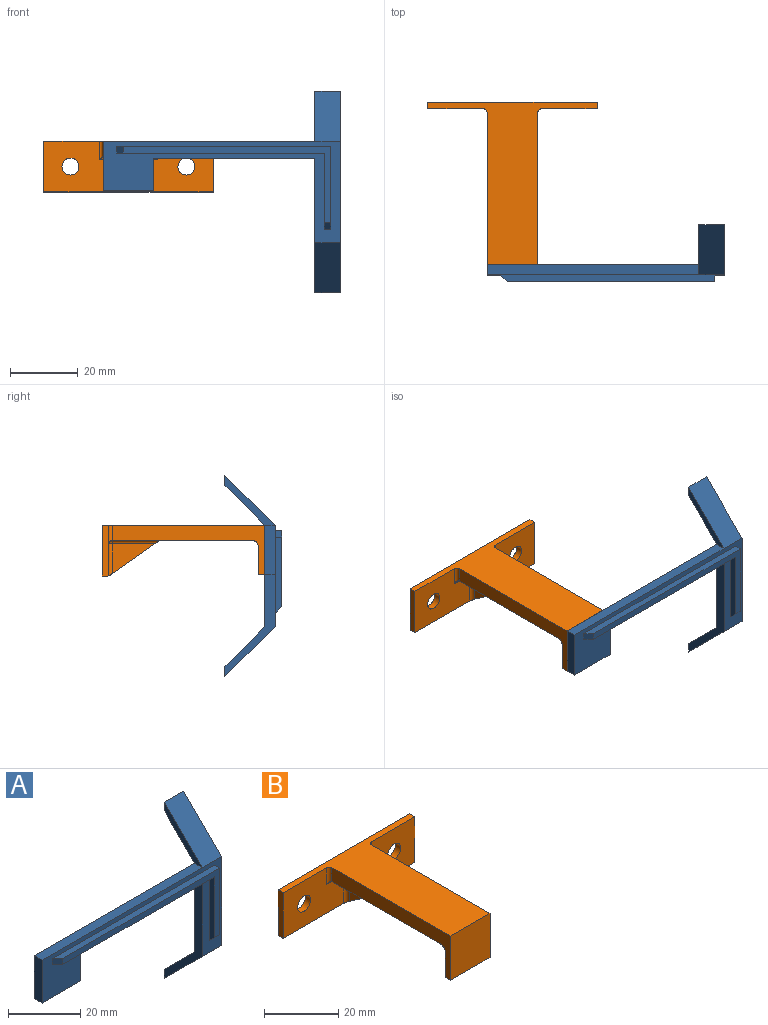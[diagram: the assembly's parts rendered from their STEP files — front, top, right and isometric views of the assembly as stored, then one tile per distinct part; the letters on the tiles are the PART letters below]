
ASSEMBLY  parts=2 mates=1
PART A: 23 faces, bbox 70x16.8x59.6 mm
  f0: plane 59.56x14.78mm, normal (1,0,0), area 169.7mm2, adj f2,f3,f4,f5,f12,f20,f21,f22
  f1: plane 14.78x14.78mm, normal (-1,0,0), area 39.8mm2, adj f2,f3,f4,f6
  f2: plane 11.78x11.78mm, normal (0,0.71,-0.71), area 124.9mm2, adj f0,f1,f4,f12
  f3: plane 14.78x14.78mm, normal (0,-0.71,0.71), area 156.8mm2, adj f0,f1,f4,f5
  f4: plane 7.5x3mm, normal (0,1,0), area 22.5mm2, adj f0,f1,f2,f3
  f5: plane 70x30mm, normal (0,-1,0), area 508.5mm2, adj f0,f3,f6,f7,f8,f9,f10,f11
  f6: plane 62.5x3mm, normal (0,0,1), area 187.5mm2, adj f1,f5,f7,f12
  f7: plane 14.5x3mm, normal (-1,0,0), area 43.5mm2, adj f5,f6,f8,f12
  f8: plane 15x3mm, normal (0,0,-1), area 45mm2, adj f5,f7,f9,f12
  f9: plane 9.5x3mm, normal (1,0,0), area 28.5mm2, adj f5,f8,f10,f12
  f10: plane 47.5x3mm, normal (0,0,-1), area 142.5mm2, adj f5,f9,f11,f12
  f11: plane 39.78x14.78mm, normal (-1,0,0), area 114.8mm2, adj f5,f10,f12,f20,f21,f22
  f12: plane 70x30mm, normal (0,1,0), area 680mm2, adj f0,f2,f6,f7,f8,f9,f10,f11
  f13: plane 63.25x2mm, normal (0,0,1), area 124.5mm2, adj f5,f16,f17,f19
  f14: plane 61.25x2mm, normal (0,0,-1), area 120.5mm2, adj f5,f15,f17,f19
  f15: plane 22.5x2mm, normal (-1,0,0), area 43mm2, adj f5,f14,f17,f18
  f16: plane 24.5x2mm, normal (1,0,0), area 47mm2, adj f5,f13,f17,f18
  f17: plane 61.25x22.5mm, normal (0,-1,0), area 163.5mm2, adj f13,f14,f15,f16,f18,f19
  f18: plane 2x2mm, normal (0,-0.71,-0.71), area 5.7mm2, adj f5,f15,f16,f17
  f19: plane 2x2mm, normal (-0.71,-0.71,0), area 5.7mm2, adj f5,f13,f14,f17
  f20: plane 11.78x11.78mm, normal (0,0.71,0.71), area 124.9mm2, adj f0,f11,f12,f22
  f21: plane 14.78x14.78mm, normal (0,-0.71,-0.71), area 156.8mm2, adj f0,f5,f11,f22
  f22: plane 7.5x3mm, normal (0,1,0), area 22.5mm2, adj f0,f11,f20,f21
PART B: 31 faces, bbox 50.2x48.2x15.2 mm
  f0: plane 41.03x15mm, normal (0,0,-1), area 558.3mm2, adj f12,f13,f18,f21,f22,f23,f24,f25
  f1: plane 12.57x8.8mm, normal (-1,0,0), area 55.3mm2, adj f15,f25,f29
  f2: plane 12.57x8.8mm, normal (1,0,0), area 55.3mm2, adj f15,f22,f28
  f3: plane 23x14.95mm, normal (0,-1,0), area 288.4mm2, adj f5,f6,f8,f20,f24,f29,f30
  f4: plane 23x14.95mm, normal (0,-1,0), area 288.4mm2, adj f5,f9,f10,f19,f23,f28,f30
  f5: plane 50x48mm, normal (0,0,1), area 790.4mm2, adj f3,f4,f6,f10,f11,f12,f13,f14
  f6: plane 15x2mm, normal (-1,0,0), area 30mm2, adj f3,f5,f7,f11,f30
  f7: plane 50x1.68mm, normal (0,0,-1), area 84.2mm2, adj f6,f10,f11,f30
  f8: cylinder r=2.5mm len=5mm, axis (0,1,0), area 31.4mm2, adj f3,f11
  f9: cylinder r=2.5mm len=5mm, axis (0,1,0), area 31.4mm2, adj f4,f11
  f10: plane 15x2mm, normal (1,0,0), area 30mm2, adj f4,f5,f7,f11,f30
  f11: plane 50x15mm, normal (0,1,0), area 710.7mm2, adj f5,f6,f7,f8,f9,f10
  f12: plane 45.21x14.71mm, normal (1,0,0), area 222.8mm2, adj f0,f5,f14,f16,f17,f18,f19
  f13: plane 45.21x14.71mm, normal (-1,0,0), area 222.8mm2, adj f0,f5,f14,f16,f17,f18,f20
  f14: plane 15x14.5mm, normal (0,-1,0), area 217.5mm2, adj f5,f12,f13,f17
  f15: plane 14.64x10.29mm, normal (0,-0.57,-0.82), area 35.9mm2, adj f1,f2,f21,f22,f25,f28,f29,f30
  f16: plane 15x8mm, normal (0,1,0), area 120mm2, adj f12,f13,f17,f18
  f17: plane 15x1.97mm, normal (0,0,-1), area 29.5mm2, adj f12,f13,f14,f16
  f18: bspline ~16.5x2mm, area 48.8mm2, adj f0,f12,f13,f16
  f19: cylinder r=1mm len=5.5mm, axis (0,0,1), area 7.9mm2, adj f4,f5,f12,f23
  f20: cylinder r=1mm len=5.5mm, axis (0,0,-1), area 7.9mm2, adj f3,f5,f13,f24
  f21: cylinder r=1mm len=4mm, axis (-1,0,0), area 2.1mm2, adj f0,f15,f22,f25
  f22: cylinder r=1mm len=14.32mm, axis (0,-1,0), area 21.2mm2, adj f0,f2,f15,f21,f26
  f23: cylinder r=1mm len=6.5mm, axis (1,0,0), area 9.4mm2, adj f0,f4,f19,f26
  f24: cylinder r=1mm len=6.5mm, axis (1,0,0), area 9.4mm2, adj f0,f3,f20,f27
  f25: cylinder r=1mm len=14.32mm, axis (0,1,0), area 21.2mm2, adj f0,f1,f15,f21,f27
  f26: sphere r=1mm, area 2.1mm2, adj f22,f23,f28
  f27: sphere r=1mm, area 1mm2, adj f24,f25,f29
  f28: cylinder r=1mm len=9.45mm, axis (0,0,1), area 14.5mm2, adj f2,f4,f15,f26,f30
  f29: cylinder r=1mm len=9.45mm, axis (0,0,-1), area 14.5mm2, adj f1,f3,f15,f27,f30
  f30: cylinder r=1mm len=50mm, axis (1,0,0), area 17mm2, adj f3,f4,f6,f7,f10,f15,f28,f29
PLACE A t=(-5.77,-40.48,8.32)mm
PLACE B t=(-16.24,7.52,-3.92)mm
MATE fastened A.f12 <-> B.f14  axis (0,1,0) through (-12.76,-40.48,0.24)mm
